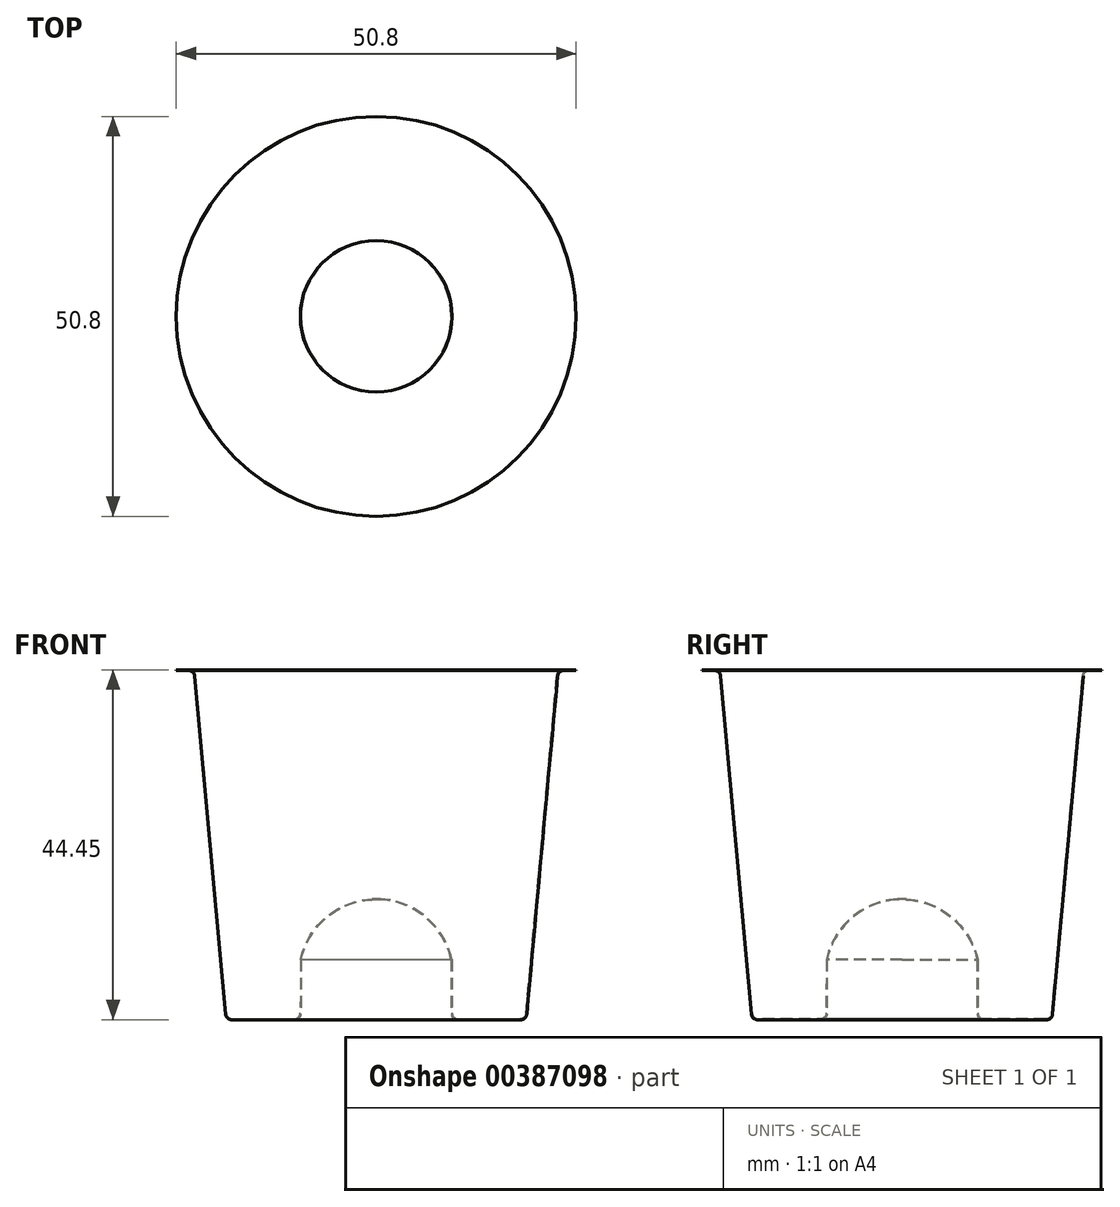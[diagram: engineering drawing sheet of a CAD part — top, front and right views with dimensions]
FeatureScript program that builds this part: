
annotation { "Feature Type Name" : "Feature", "Feature Type Description" : "" }
export const myFeature = defineFeature(function(context is Context, id is Id, definition is map)
    precondition{}
    {
        {
            var Q0;
            Q0=qCreatedBy(makeId("Front.planeOp"),FACE);
            var sketch = newSketch(context, id + "F0", { "sketchPlane" : qUnion([Q0])});
            skLineSegment(sketch, "E0", {"start": v(23.11, 29.1) * mm, "end": v(25.4, 29.1) * mm});
            skLineSegment(sketch, "E1", {"start": v(25.4, 29.1) * mm, "end": v(25.4, 29.21) * mm});
            skLineSegment(sketch, "E2", {"start": v(25.4, 29.21) * mm, "end": v(0, 29.21) * mm});
            skPoint(sketch, "E3.start.orphan", {"position": v(19.07, -15.24) * mm});
            skLineSegment(sketch, "E4", {"start": v(19.07, -15.24) * mm, "end": v(23.11, 29.1) * mm});
            skLineSegment(sketch, "E5", {"start": v(0, 29.21) * mm, "end": v(0, 0) * mm});
            skLineSegment(sketch, "E6", {"start": v(19.07, -15.24) * mm, "end": v(9.54, -15.24) * mm});
            skLineSegment(sketch, "E7", {"start": v(0, 0) * mm, "end": v(0.55, 0) * mm});
            skLineSegment(sketch, "E8", {"start": v(9.53, -7.62) * mm, "end": v(9.54, -15.24) * mm});
            skArc(sketch, "E9", {"start": v(0.55, 0) * mm, "mid": v(0.28, 0.01) * mm, "end": v(0, 0.02) * mm});
            skArc(sketch, "E10", {"start": v(0.55, 0) * mm, "mid": v(6.32, -2.3) * mm, "end": v(9.53, -7.62) * mm});
            skSolve(sketch);
        }
        {
            var Q0;
            Q0=makeQuery(id+"F0.imprint","IMPRINT",FACE,{"disambiguationData":[TD([[makeQuery(id+"F0.imprint","IMPRINT",EDGE,{"derivedFrom":sQuery(id+"F0.wireOp",EDGE,"E0")}),1.0]])]});
            var Q1;
            Q1=makeQuery(id+"F0.imprint","IMPRINT",FACE,{"disambiguationData":[TD([[makeQuery(id+"F0.imprint","IMPRINT",EDGE,{"derivedFrom":sQuery(id+"F0.wireOp",EDGE,"E4")}),1.0]])]});
            var Q2;
            Q2=sQuery(id+"F0.wireOp",EDGE,"E5");
            revolve(context, id + "F1", {"entities" : qUnion([Q0, Q1]), "axis" : qUnion([Q2]), "revolveType" : RevolveType.FULL});
        }
        {
            var Q0;
            Q0=makeQuery(id+"F1.opRevolve","SWEPT_FACE",FACE,{"disambiguationData":[OSD([sQuery(id+"F0.wireOp",EDGE,"E2")])]});
            shell(context, id + "F2", {"entities" : qUnion([Q0]), "thickness" : 0.1 * mm});
        }
        {
            var Q0;
            Q0=makeQuery(id+"F2.opShell","OFFSET_EDGE",EDGE,{"disambiguationData":[OSD([sQuery(id+"F0.wireOp",EDGE,"E4"),sQuery(id+"F0.wireOp",EDGE,"E6")])]});
            var Q1;
            Q1=makeQuery(id+"F1.opRevolve","SWEPT_EDGE",EDGE,{"disambiguationData":[OSD([sQuery(id+"F0.wireOp",EDGE,"E4"),sQuery(id+"F0.wireOp",EDGE,"E6")])]});
            fillet(context, id + "F3", {"entities" : qUnion([Q0, Q1]), "radius" : 0.76 * mm, "allowEdgeOverflow" : false});
        }
        {
            var Q0;
            Q0=makeQuery(id+"F1.opRevolve","SWEPT_EDGE",EDGE,{"disambiguationData":[OSD([sQuery(id+"F0.wireOp",EDGE,"E0"),sQuery(id+"F0.wireOp",EDGE,"E4")])]});
            var Q1;
            Q1=makeQuery(id+"F2.opShell","OFFSET_EDGE",EDGE,{"disambiguationData":[OSD([sQuery(id+"F0.wireOp",EDGE,"E0"),sQuery(id+"F0.wireOp",EDGE,"E4")])]});
            fillet(context, id + "F4", {"entities" : qUnion([Q0, Q1]), "radius" : 0.76 * mm, "allowEdgeOverflow" : false});
        }
        {
            var Q0;
            Q0=makeQuery(id+"F2.opShell","OFFSET_EDGE",EDGE,{"disambiguationData":[OSD([sQuery(id+"F0.wireOp",EDGE,"E6"),sQuery(id+"F0.wireOp",EDGE,"E8")])]});
            var Q1;
            Q1=makeQuery(id+"F1.opRevolve","SWEPT_EDGE",EDGE,{"disambiguationData":[OSD([sQuery(id+"F0.wireOp",EDGE,"E6"),sQuery(id+"F0.wireOp",EDGE,"E8")])]});
            fillet(context, id + "F5", {"entities" : qUnion([Q0, Q1]), "radius" : 0.76 * mm, "tangentPropagation" : true, "allowEdgeOverflow" : false});
        }
    });
